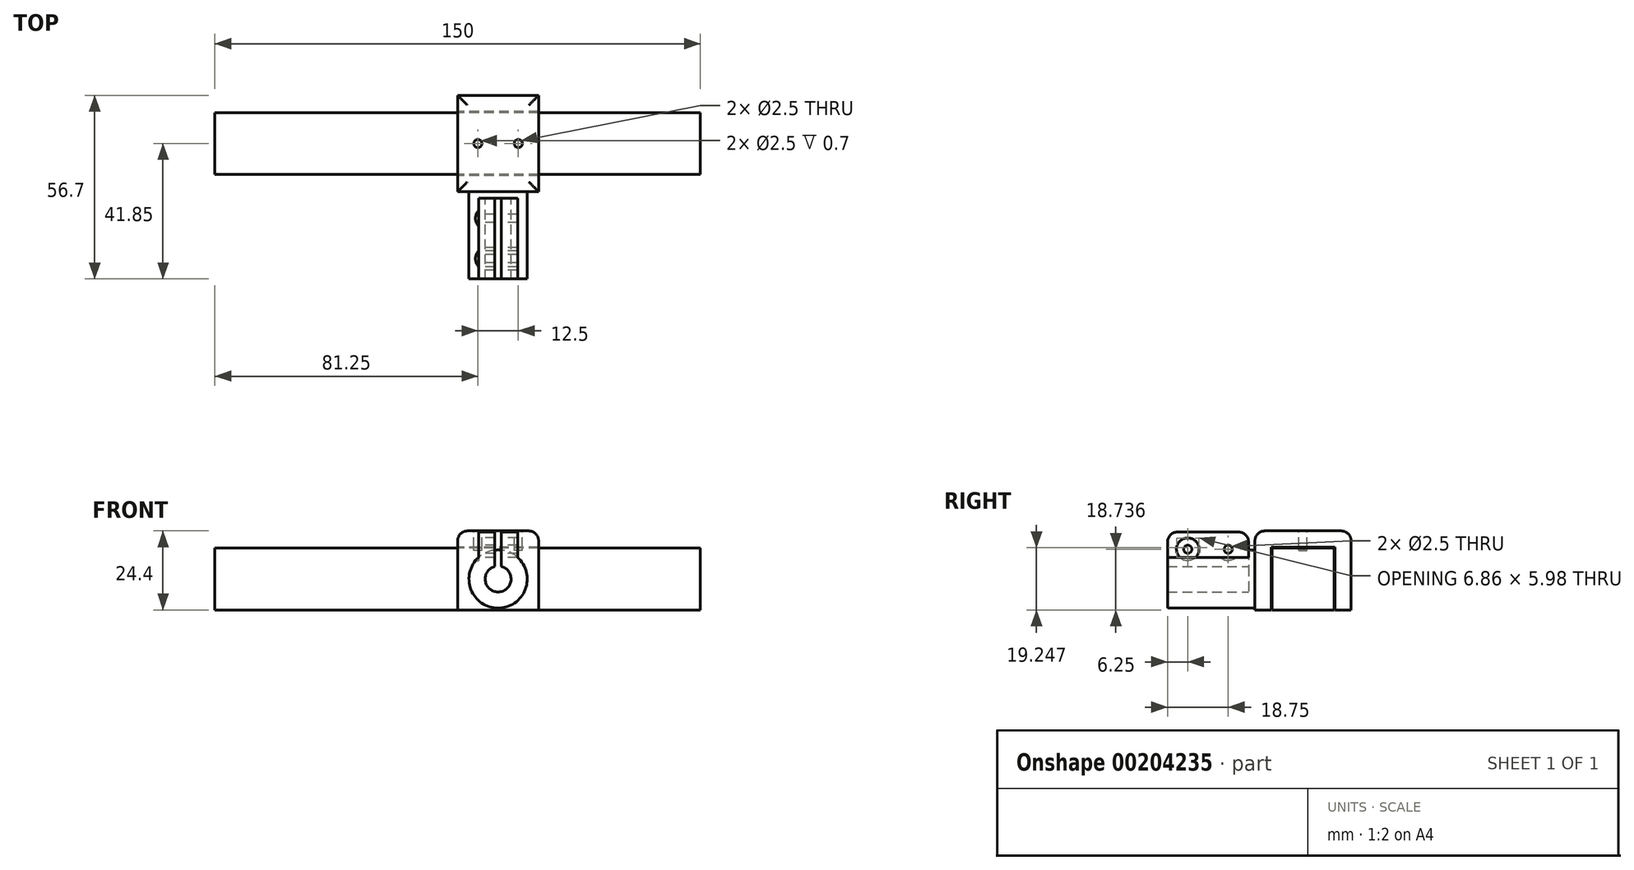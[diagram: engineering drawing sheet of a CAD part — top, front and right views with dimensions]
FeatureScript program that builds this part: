
annotation { "Feature Type Name" : "Feature", "Feature Type Description" : "" }
export const myFeature = defineFeature(function(context is Context, id is Id, definition is map)
    precondition{}
    {
        {
            var Q0;
            Q0=qCreatedBy(makeId("Right.planeOp"),FACE);
            var sketch = newSketch(context, id + "F0", { "sketchPlane" : qUnion([Q0])});
            skLineSegment(sketch, "E0.bottom", {"start": v(0, 0) * mm, "end": v(19.1, 0) * mm});
            skLineSegment(sketch, "E0.top", {"start": v(0, 19.1) * mm, "end": v(19.1, 19.1) * mm});
            skLineSegment(sketch, "E0.left", {"start": v(0, 0) * mm, "end": v(0, 19.1) * mm});
            skLineSegment(sketch, "E0.right", {"start": v(19.1, 0) * mm, "end": v(19.1, 19.1) * mm});
            skLineSegment(sketch, "E1", {"start": v(19.1, 0) * mm, "end": v(19.4, 0) * mm, "construction": true});
            skLineSegment(sketch, "E2", {"start": v(0, 19.1) * mm, "end": v(0, 19.4) * mm, "construction": true});
            skLineSegment(sketch, "E3", {"start": v(0, 0) * mm, "end": v(-0.3, 0) * mm, "construction": true});
            skLineSegment(sketch, "E4", {"start": v(-0.3, 0) * mm, "end": v(-0.3, 19.4) * mm});
            skLineSegment(sketch, "E5", {"start": v(19.4, 0) * mm, "end": v(19.4, 19.4) * mm});
            skLineSegment(sketch, "E6", {"start": v(0, 19.4) * mm, "end": v(19.4, 19.4) * mm});
            skLineSegment(sketch, "E7", {"start": v(0, 19.4) * mm, "end": v(-0.3, 19.4) * mm});
            skLineSegment(sketch, "E8", {"start": v(19.4, 0) * mm, "end": v(24.4, 0) * mm});
            skLineSegment(sketch, "E9", {"start": v(24.4, 0) * mm, "end": v(24.4, 24.4) * mm});
            skLineSegment(sketch, "E10", {"start": v(24.4, 24.4) * mm, "end": v(-5.3, 24.4) * mm});
            skLineSegment(sketch, "E11", {"start": v(-5.3, 24.4) * mm, "end": v(-5.3, 0) * mm});
            skLineSegment(sketch, "E12", {"start": v(-5.3, 0) * mm, "end": v(-0.3, 0) * mm});
            skLineSegment(sketch, "E13", {"start": v(-0.3, 19.4) * mm, "end": v(-0.3, 24.4) * mm, "construction": true});
            skSolve(sketch);
        }
        {
            var Q0;
            Q0=makeQuery(id+"F0.imprint","IMPRINT",FACE,{"disambiguationData":[TD([[makeQuery(id+"F0.imprint","IMPRINT",EDGE,{"derivedFrom":sQuery(id+"F0.wireOp",EDGE,"E0.bottom")}),1.0]])]});
            extrude(context, id + "F1", {"entities" : qUnion([Q0]), "endBound" : BoundingType.SYMMETRIC, "depth" : 150 * mm});
        }
        {
            var Q0;
            Q0=makeQuery(id+"F0.imprint","IMPRINT",FACE,{"disambiguationData":[TD([[makeQuery(id+"F0.imprint","IMPRINT",EDGE,{"derivedFrom":sQuery(id+"F0.wireOp",EDGE,"E4")}),1.0]])]});
            extrude(context, id + "F2", {"entities" : qUnion([Q0]), "depth" : 25 * mm});
        }
        {
            var Q0;
            Q0=makeQuery(id+"F2.opExtrude","SWEPT_FACE",FACE,{"disambiguationData":[OSD([sQuery(id+"F0.wireOp",EDGE,"E11")])]});
            var sketch = newSketch(context, id + "F3", { "sketchPlane" : qUnion([Q0])});
            skCircle(sketch, "E14", {"center": v(12.5, 9.55) * mm, "radius": 9 * mm});
            skSolve(sketch);
        }
        {
            var Q0;
            Q0 = qSketchRegion(id + "F3", true);
            extrude(context, id + "F4", {"entities" : qUnion([Q0]), "operationType" : NewBodyOperationType.ADD, "depth" : 2 * mm});
        }
        {
            var Q0;
            Q0=makeQuery(id+"F4.opExtrude","CAP_FACE",FACE,{"disambiguationData":[OSD([sQuery(id+"F3.wireOp",EDGE,"E14")])],"isStart":false});
            var sketch = newSketch(context, id + "F5", { "sketchPlane" : qUnion([Q0])});
            skArc(sketch, "E15", {"start": v(11.5, 13.42) * mm, "mid": v(12.5, 5.55) * mm, "end": v(13.5, 13.42) * mm});
            skPoint(sketch, "E15.centerSnap0", {"position": v(12.5, 0) * mm});
            skArc(sketch, "E16", {"start": v(6.5, 16.26) * mm, "mid": v(12.5, 0.55) * mm, "end": v(18.5, 16.26) * mm});
            skLineSegment(sketch, "E17", {"start": v(12.5, 9.55) * mm, "end": v(12.5, 24.4) * mm, "construction": true});
            skLineSegment(sketch, "E18", {"start": v(12.5, 18.55) * mm, "end": v(13.5, 18.55) * mm, "construction": true});
            skLineSegment(sketch, "E19", {"start": v(13.5, 18.55) * mm, "end": v(12.5, 18.55) * mm, "construction": true});
            skLineSegment(sketch, "E20", {"start": v(11.5, 18.55) * mm, "end": v(12.5, 18.55) * mm, "construction": true});
            skLineSegment(sketch, "E21", {"start": v(11.5, 18.55) * mm, "end": v(11.5, 13.42) * mm});
            skLineSegment(sketch, "E22", {"start": v(13.5, 18.55) * mm, "end": v(13.5, 13.42) * mm});
            skLineSegment(sketch, "E23", {"start": v(11.5, 18.55) * mm, "end": v(11.5, 24.05) * mm});
            skLineSegment(sketch, "E24", {"start": v(13.5, 24.05) * mm, "end": v(13.5, 18.55) * mm});
            skLineSegment(sketch, "E25", {"start": v(13.5, 24.05) * mm, "end": v(18.5, 24.05) * mm});
            skLineSegment(sketch, "E26", {"start": v(18.5, 24.05) * mm, "end": v(18.5, 16.26) * mm});
            skLineSegment(sketch, "E27", {"start": v(11.5, 24.05) * mm, "end": v(6.5, 24.05) * mm});
            skLineSegment(sketch, "E28", {"start": v(6.5, 24.05) * mm, "end": v(6.5, 16.26) * mm});
            skSolve(sketch);
        }
        {
            var Q0;
            Q0 = qSketchRegion(id + "F5", true);
            extrude(context, id + "F6", {"entities" : qUnion([Q0]), "operationType" : NewBodyOperationType.ADD, "depth" : 25 * mm});
        }
        {
            var Q0;
            Q0=makeQuery(id+"F6.opExtrude","CAP_FACE",FACE,{"disambiguationData":[OSD([sQuery(id+"F5.wireOp",EDGE,"E15"),sQuery(id+"F5.wireOp",EDGE,"E16"),sQuery(id+"F5.wireOp",EDGE,"E21"),sQuery(id+"F5.wireOp",EDGE,"E22"),sQuery(id+"F5.wireOp",EDGE,"E23"),sQuery(id+"F5.wireOp",EDGE,"E24"),sQuery(id+"F5.wireOp",EDGE,"E25"),sQuery(id+"F5.wireOp",EDGE,"E26"),sQuery(id+"F5.wireOp",EDGE,"E27"),sQuery(id+"F5.wireOp",EDGE,"E28")])],"isStart":false});
            var sketch = newSketch(context, id + "F7", { "sketchPlane" : qUnion([Q0])});
            skLineSegment(sketch, "E29", {"start": v(11.5, 18.74) * mm, "end": v(6.5, 18.74) * mm, "construction": true});
            skSolve(sketch);
        }
        {
            var Q0;
            Q0=makeQuery(id+"F6.opExtrude","SWEPT_FACE",FACE,{"disambiguationData":[OSD([sQuery(id+"F5.wireOp",EDGE,"E28")])]});
            var sketch = newSketch(context, id + "F8", { "sketchPlane" : qUnion([Q0])});
            skLineSegment(sketch, "E30", {"start": v(32.3, 18.74) * mm, "end": v(7.3, 18.74) * mm, "construction": true});
            skLineSegment(sketch, "E31", {"start": v(19.8, 24.05) * mm, "end": v(19.8, 18.74) * mm, "construction": true});
            skCircle(sketch, "E32", {"center": v(13.55, 18.74) * mm, "radius": 1.25 * mm});
            skCircle(sketch, "E33", {"center": v(13.55, 18.74) * mm, "radius": 3.5 * mm});
            skCircle(sketch, "E34.MirrorC", {"center": v(26.05, 18.74) * mm, "radius": 3.5 * mm});
            skCircle(sketch, "E35.MirrorC", {"center": v(26.05, 18.74) * mm, "radius": 1.25 * mm});
            skSolve(sketch);
        }
        {
            var Q0;
            Q0 = qSketchRegion(id + "F8", true);
            extrude(context, id + "F9", {"entities" : qUnion([Q0]), "operationType" : NewBodyOperationType.REMOVE, "depth" : 25 * mm});
        }
        {
            var Q0;
            Q0=makeQuery(id+"F8.imprint","IMPRINT",FACE,{"disambiguationData":[TD([[makeQuery(id+"F8.imprint","IMPRINT",EDGE,{"derivedFrom":sQuery(id+"F8.wireOp",EDGE,"E32")}),1.0]])]});
            var Q1;
            Q1=makeQuery(id+"F8.imprint","IMPRINT",FACE,{"disambiguationData":[TD([[makeQuery(id+"F8.imprint","IMPRINT",EDGE,{"derivedFrom":sQuery(id+"F8.wireOp",EDGE,"E35.MirrorC")}),-1.0]])]});
            var Q2;
            Q2=sQuery(id+"F8.wireOp",EDGE,"E32");
            var Q3;
            Q3=sQuery(id+"F8.wireOp",EDGE,"E35.MirrorC");
            extrude(context, id + "F10", {"entities" : qUnion([Q0, Q1]), "operationType" : NewBodyOperationType.REMOVE, "surfaceEntities" : qUnion([Q2, Q3]), "oppositeDirection" : true, "depth" : 25 * mm});
        }
        {
            var Q0;
            Q0=makeQuery(id+"F2.opExtrude","SWEPT_FACE",FACE,{"disambiguationData":[OSD([sQuery(id+"F0.wireOp",EDGE,"E10")])]});
            var sketch = newSketch(context, id + "F11", { "sketchPlane" : qUnion([Q0])});
            skLineSegment(sketch, "E36", {"start": v(12.5, -5.3) * mm, "end": v(12.5, 24.4) * mm, "construction": true});
            skCircle(sketch, "E37", {"center": v(18.75, 9.55) * mm, "radius": 1.25 * mm});
            skLineSegment(sketch, "E38", {"start": v(12.5, 9.55) * mm, "end": v(25, 9.55) * mm, "construction": true});
            skCircle(sketch, "E39.MirrorC", {"center": v(6.25, 9.55) * mm, "radius": 1.25 * mm});
            skSolve(sketch);
        }
        {
            var Q0;
            Q0 = qSketchRegion(id + "F11", true);
            extrude(context, id + "F12", {"entities" : qUnion([Q0]), "operationType" : NewBodyOperationType.REMOVE, "oppositeDirection" : true, "depth" : 6 * mm});
        }
        {
            var Q0;
            Q0=makeQuery(id+"F2.opExtrude","CAP_EDGE",EDGE,{"disambiguationData":[OSD([sQuery(id+"F0.wireOp",EDGE,"E10")])],"isStart":false});
            var Q1;
            Q1=makeQuery(id+"F2.opExtrude","SWEPT_EDGE",EDGE,{"disambiguationData":[OSD([sQuery(id+"F0.wireOp",EDGE,"E9"),sQuery(id+"F0.wireOp",EDGE,"E10")])]});
            var Q2;
            Q2=makeQuery(id+"F2.opExtrude","CAP_EDGE",EDGE,{"disambiguationData":[OSD([sQuery(id+"F0.wireOp",EDGE,"E10")])],"isStart":true});
            var Q3;
            Q3=makeQuery(id+"F2.opExtrude","SWEPT_EDGE",EDGE,{"disambiguationData":[OSD([sQuery(id+"F0.wireOp",EDGE,"E10"),sQuery(id+"F0.wireOp",EDGE,"E11")])]});
            var Q4;
            Q4=makeQuery(id+"F6.opExtrude","CAP_EDGE",EDGE,{"disambiguationData":[OSD([sQuery(id+"F5.wireOp",EDGE,"E25")])],"isStart":false});
            var Q5;
            Q5=makeQuery(id+"F6.opExtrude","CAP_EDGE",EDGE,{"disambiguationData":[OSD([sQuery(id+"F5.wireOp",EDGE,"E27")])],"isStart":false});
            var Q6;
            Q6=makeQuery(id+"F6.opExtrude","CAP_EDGE",EDGE,{"disambiguationData":[OSD([sQuery(id+"F5.wireOp",EDGE,"E27")])],"isStart":true});
            var Q7;
            Q7=makeQuery(id+"F6.opExtrude","CAP_EDGE",EDGE,{"disambiguationData":[OSD([sQuery(id+"F5.wireOp",EDGE,"E25")])],"isStart":true});
            fillet(context, id + "F13", {"entities" : qUnion([Q0, Q1, Q2, Q3, Q4, Q5, Q6, Q7]), "radius" : 3 * mm, "tangentPropagation" : true, "allowEdgeOverflow" : false});
        }
    });
